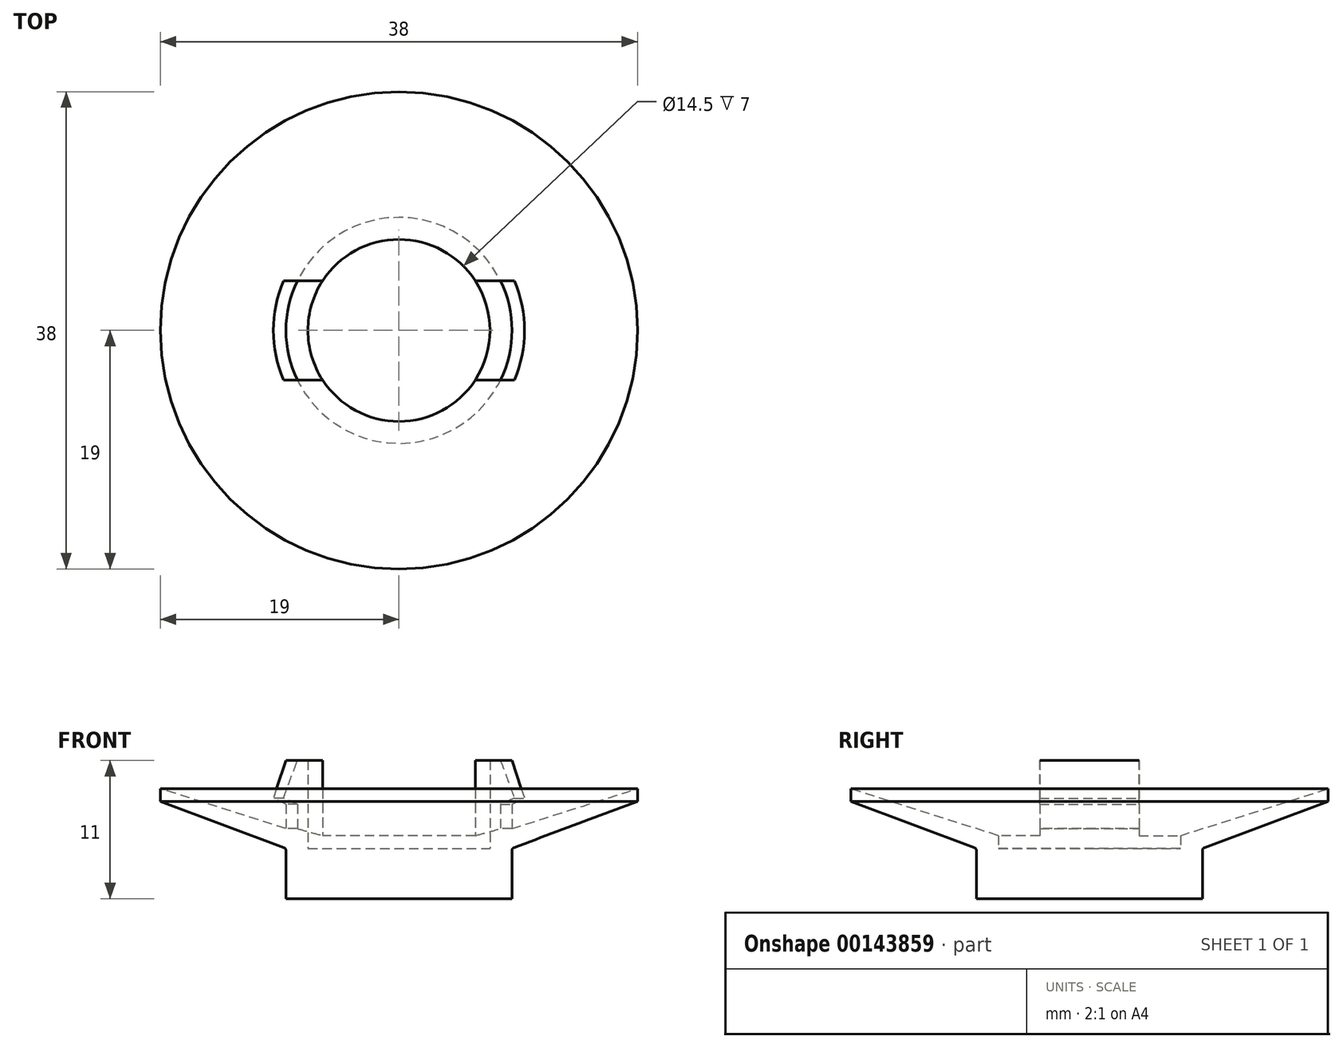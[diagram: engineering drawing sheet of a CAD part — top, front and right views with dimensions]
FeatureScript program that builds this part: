
annotation { "Feature Type Name" : "Feature", "Feature Type Description" : "" }
export const myFeature = defineFeature(function(context is Context, id is Id, definition is map)
    precondition{}
    {
        {
            var Q0;
            Q0=qCreatedBy(makeId("Front.planeOp"),FACE);
            var sketch = newSketch(context, id + "F0", { "sketchPlane" : qUnion([Q0])});
            skCircle(sketch, "E0", {"center": v(95.2, 4.49) * mm, "radius": 8.75 * mm});
            skCircle(sketch, "E1", {"center": v(95.2, -8.26) * mm, "radius": 8 * mm});
            skCircle(sketch, "E2", {"center": v(95.2, -8.26) * mm, "radius": 7.5 * mm});
            skLineSegment(sketch, "E3", {"start": v(59.96, -2.26) * mm, "end": v(59.96, -0.76) * mm});
            skLineSegment(sketch, "E4", {"start": v(59.96, -0.76) * mm, "end": v(64.96, -0.26) * mm});
            skLineSegment(sketch, "E5", {"start": v(64.96, -0.26) * mm, "end": v(64.96, -0.76) * mm});
            skLineSegment(sketch, "E6", {"start": v(64.96, -0.76) * mm, "end": v(69.96, -0.26) * mm});
            skLineSegment(sketch, "E7", {"start": v(69.96, -0.26) * mm, "end": v(69.96, -0.76) * mm});
            skLineSegment(sketch, "E8", {"start": v(69.96, -0.76) * mm, "end": v(74.96, -0.26) * mm});
            skLineSegment(sketch, "E9", {"start": v(74.96, -0.26) * mm, "end": v(86.46, -0.26) * mm});
            skLineSegment(sketch, "E10", {"start": v(86.46, -0.26) * mm, "end": v(86.46, 4.49) * mm});
            skLineSegment(sketch, "E11", {"start": v(86.46, 4.49) * mm, "end": v(76.2, 8.24) * mm});
            skLineSegment(sketch, "E12", {"start": v(76.2, 8.24) * mm, "end": v(76.2, 9.24) * mm});
            skLineSegment(sketch, "E13", {"start": v(76.2, 9.24) * mm, "end": v(95.2, 9.24) * mm});
            skLineSegment(sketch, "E14", {"start": v(95.2, 9.24) * mm, "end": v(114.2, 9.24) * mm});
            skLineSegment(sketch, "E15", {"start": v(114.2, 9.24) * mm, "end": v(114.2, 8.24) * mm});
            skLineSegment(sketch, "E16", {"start": v(114.2, 8.24) * mm, "end": v(103.96, 4.49) * mm});
            skLineSegment(sketch, "E17", {"start": v(103.96, 4.49) * mm, "end": v(103.96, -0.26) * mm});
            skLineSegment(sketch, "E18", {"start": v(103.96, -0.26) * mm, "end": v(103.18, -8.98) * mm});
            skArc(sketch, "E19", {"start": v(103.18, -8.98) * mm, "mid": v(100.6, -14.17) * mm, "end": v(95.2, -16.26) * mm});
            skLineSegment(sketch, "E20", {"start": v(95.2, -16.26) * mm, "end": v(74.96, -16.26) * mm});
            skLineSegment(sketch, "E21", {"start": v(74.96, -16.26) * mm, "end": v(69.96, -15.76) * mm});
            skLineSegment(sketch, "E22", {"start": v(69.96, -15.76) * mm, "end": v(69.96, -16.26) * mm});
            skLineSegment(sketch, "E23", {"start": v(69.96, -16.26) * mm, "end": v(64.96, -15.76) * mm});
            skLineSegment(sketch, "E24", {"start": v(64.96, -15.76) * mm, "end": v(64.96, -16.26) * mm});
            skLineSegment(sketch, "E25", {"start": v(64.96, -16.26) * mm, "end": v(59.96, -15.76) * mm});
            skLineSegment(sketch, "E26", {"start": v(59.96, -15.76) * mm, "end": v(59.96, -2.26) * mm});
            skCircle(sketch, "E27", {"center": v(95.2, 34) * mm, "radius": 6.25 * mm});
            skCircle(sketch, "E28", {"center": v(95.2, 34) * mm, "radius": 7.25 * mm});
            skCircle(sketch, "E29", {"center": v(95.2, 34) * mm, "radius": 19 * mm});
            skCircle(sketch, "E30", {"center": v(95.2, 34) * mm, "radius": 3.75 * mm});
            skLineSegment(sketch, "E31", {"start": v(86.46, 4.49) * mm, "end": v(85.46, 4.85) * mm});
            skLineSegment(sketch, "E32", {"start": v(85.46, 4.85) * mm, "end": v(85.97, 6.26) * mm});
            skLineSegment(sketch, "E33", {"start": v(85.97, 6.26) * mm, "end": v(86.97, 5.9) * mm});
            skLineSegment(sketch, "E34", {"start": v(86.97, 5.9) * mm, "end": v(86.46, 4.49) * mm});
            skCircle(sketch, "E35", {"center": v(95.2, -8.26) * mm, "radius": 6.25 * mm});
            skArc(sketch, "E36", {"start": v(104.2, 30.26) * mm, "mid": v(104.96, 34) * mm, "end": v(104.2, 37.76) * mm});
            skArc(sketch, "E37", {"start": v(86.2, 37.76) * mm, "mid": v(85.46, 34) * mm, "end": v(86.2, 30.26) * mm});
            skArc(sketch, "E38", {"start": v(103.11, 30.26) * mm, "mid": v(103.96, 34) * mm, "end": v(103.11, 37.76) * mm});
            skArc(sketch, "E39", {"start": v(87.3, 37.76) * mm, "mid": v(86.46, 34) * mm, "end": v(87.3, 30.26) * mm});
            skLineSegment(sketch, "E40", {"start": v(88.96, 4.49) * mm, "end": v(87.96, 4.49) * mm});
            skLineSegment(sketch, "E41", {"start": v(87.96, 4.49) * mm, "end": v(87.96, 11.49) * mm});
            skLineSegment(sketch, "E42", {"start": v(87.96, 11.49) * mm, "end": v(86.46, 11.49) * mm});
            skLineSegment(sketch, "E43", {"start": v(86.46, 11.49) * mm, "end": v(85.46, 8.49) * mm});
            skLineSegment(sketch, "E44", {"start": v(85.46, 8.49) * mm, "end": v(86.46, 7.99) * mm});
            skLineSegment(sketch, "E45", {"start": v(86.46, 7.99) * mm, "end": v(86.46, 6.06) * mm});
            skLineSegment(sketch, "E46", {"start": v(86.46, 6.06) * mm, "end": v(76.2, 9.24) * mm});
            skLineSegment(sketch, "E47", {"start": v(64.96, -0.76) * mm, "end": v(64.96, -15.76) * mm});
            skLineSegment(sketch, "E48", {"start": v(69.96, -0.76) * mm, "end": v(69.96, -15.76) * mm});
            skLineSegment(sketch, "E49", {"start": v(59.96, -2.01) * mm, "end": v(88.96, -2.01) * mm});
            skLineSegment(sketch, "E50", {"start": v(88.96, -2.01) * mm, "end": v(88.96, 4.49) * mm});
            skLineSegment(sketch, "E51", {"start": v(101.41, 37.76) * mm, "end": v(104.2, 37.76) * mm});
            skLineSegment(sketch, "E52", {"start": v(104.2, 30.26) * mm, "end": v(101.41, 30.26) * mm});
            skLineSegment(sketch, "E53", {"start": v(86.2, 37.76) * mm, "end": v(89, 37.76) * mm});
            skLineSegment(sketch, "E54", {"start": v(89, 30.26) * mm, "end": v(86.2, 30.26) * mm});
            skLineSegment(sketch, "E55", {"start": v(86.46, 6.06) * mm, "end": v(87.3, 6.06) * mm});
            skLineSegment(sketch, "E56", {"start": v(89, 4.49) * mm, "end": v(89, 11.49) * mm});
            skLineSegment(sketch, "E57", {"start": v(89, 11.49) * mm, "end": v(87.3, 11.49) * mm});
            skLineSegment(sketch, "E58", {"start": v(87.3, 11.49) * mm, "end": v(86.46, 8.49) * mm});
            skLineSegment(sketch, "E59", {"start": v(86.46, 8.49) * mm, "end": v(87.3, 7.99) * mm});
            skLineSegment(sketch, "E60", {"start": v(87.3, 7.99) * mm, "end": v(87.3, 6.06) * mm});
            skLineSegment(sketch, "E61", {"start": v(101.46, 4.49) * mm, "end": v(102.46, 4.49) * mm});
            skLineSegment(sketch, "E62", {"start": v(102.46, 4.49) * mm, "end": v(102.46, 11.49) * mm});
            skLineSegment(sketch, "E63", {"start": v(102.46, 11.49) * mm, "end": v(103.96, 11.49) * mm});
            skLineSegment(sketch, "E64", {"start": v(103.96, 11.49) * mm, "end": v(104.96, 8.49) * mm});
            skLineSegment(sketch, "E65", {"start": v(104.96, 8.49) * mm, "end": v(103.96, 7.99) * mm});
            skLineSegment(sketch, "E66", {"start": v(103.96, 7.99) * mm, "end": v(103.96, 6.06) * mm});
            skLineSegment(sketch, "E67", {"start": v(103.96, 6.06) * mm, "end": v(114.2, 9.24) * mm});
            skLineSegment(sketch, "E68", {"start": v(101.46, 4.49) * mm, "end": v(101.46, -8.26) * mm});
            skArc(sketch, "E69", {"start": v(101.46, -8.26) * mm, "mid": v(99.63, -12.68) * mm, "end": v(95.2, -14.51) * mm});
            skLineSegment(sketch, "E70", {"start": v(95.2, -14.51) * mm, "end": v(59.96, -14.51) * mm});
            skLineSegment(sketch, "E71", {"start": v(103.18, -8.98) * mm, "end": v(101.46, -8.98) * mm});
            skLineSegment(sketch, "E72", {"start": v(101.46, -8.98) * mm, "end": v(101.46, 4.49) * mm});
            skLineSegment(sketch, "E73", {"start": v(102.46, 4.49) * mm, "end": v(102.46, 5.59) * mm});
            skLineSegment(sketch, "E74", {"start": v(102.46, 5.59) * mm, "end": v(114.2, 9.24) * mm});
            skLineSegment(sketch, "E75", {"start": v(103.96, 7.99) * mm, "end": v(103.96, 5.4) * mm});
            skLineSegment(sketch, "E76", {"start": v(103.96, 5.4) * mm, "end": v(102.46, 3.7) * mm});
            skLineSegment(sketch, "E77", {"start": v(102.46, 3.7) * mm, "end": v(102.46, 11.49) * mm});
            skLineSegment(sketch, "E78", {"start": v(59.96, -14.51) * mm, "end": v(95.2, -14.51) * mm});
            skArc(sketch, "E79", {"start": v(95.2, -14.51) * mm, "mid": v(99.63, -12.68) * mm, "end": v(101.46, -8.26) * mm});
            skLineSegment(sketch, "E80", {"start": v(101.46, -8.26) * mm, "end": v(103.2, -8.26) * mm});
            skArc(sketch, "E81", {"start": v(103.2, -8.26) * mm, "mid": v(100.86, -13.92) * mm, "end": v(95.2, -16.26) * mm});
            skLineSegment(sketch, "E82", {"start": v(59.96, -15.76) * mm, "end": v(59.96, -14.51) * mm});
            skLineSegment(sketch, "E83", {"start": v(54, -8.26) * mm, "end": v(95.2, -8.26) * mm});
            skArc(sketch, "E84", {"start": v(95.2, -8.26) * mm, "mid": v(95.2, -8.26) * mm, "end": v(95.2, -8.26) * mm});
            skLineSegment(sketch, "E85", {"start": v(95.2, -8.26) * mm, "end": v(95.2, 13.24) * mm});
            skCircle(sketch, "E86", {"center": v(59.96, -8.26) * mm, "radius": 6.25 * mm});
            skArc(sketch, "E87", {"start": v(593.24, 411.17) * mm, "mid": v(593.34, 410.87) * mm, "end": v(593.66, 410.83) * mm});
            skArc(sketch, "E88", {"start": v(593.82, 411.03) * mm, "mid": v(593.72, 411.33) * mm, "end": v(593.4, 411.37) * mm});
            skLineSegment(sketch, "E89", {"start": v(593.83, 411.13) * mm, "end": v(594.01, 411.35) * mm});
            skLineSegment(sketch, "E90", {"start": v(593.8, 411.25) * mm, "end": v(593.93, 411.42) * mm});
            skLineSegment(sketch, "E91", {"start": v(593.72, 411.33) * mm, "end": v(593.85, 411.49) * mm});
            skLineSegment(sketch, "E92", {"start": v(593.62, 411.39) * mm, "end": v(593.76, 411.56) * mm});
            skLineSegment(sketch, "E93", {"start": v(593.5, 411.4) * mm, "end": v(593.69, 411.62) * mm});
            skLineSegment(sketch, "E94", {"start": v(59.96, -42.26) * mm, "end": v(59.96, -40.76) * mm});
            skLineSegment(sketch, "E95", {"start": v(59.96, -40.76) * mm, "end": v(64.96, -40.26) * mm});
            skLineSegment(sketch, "E96", {"start": v(64.96, -40.26) * mm, "end": v(64.96, -40.76) * mm});
            skLineSegment(sketch, "E97", {"start": v(64.96, -40.76) * mm, "end": v(69.96, -40.26) * mm});
            skLineSegment(sketch, "E98", {"start": v(69.96, -40.26) * mm, "end": v(69.96, -40.76) * mm});
            skLineSegment(sketch, "E99", {"start": v(69.96, -40.76) * mm, "end": v(74.96, -40.26) * mm});
            skLineSegment(sketch, "E100", {"start": v(74.96, -40.26) * mm, "end": v(86.46, -40.26) * mm});
            skLineSegment(sketch, "E101", {"start": v(86.46, -40.26) * mm, "end": v(86.46, -35.51) * mm});
            skLineSegment(sketch, "E102", {"start": v(86.46, -35.51) * mm, "end": v(76.2, -31.76) * mm});
            skLineSegment(sketch, "E103", {"start": v(76.2, -31.76) * mm, "end": v(76.2, -30.76) * mm});
            skLineSegment(sketch, "E104", {"start": v(76.2, -30.76) * mm, "end": v(95.2, -30.76) * mm});
            skLineSegment(sketch, "E105", {"start": v(95.2, -30.76) * mm, "end": v(114.2, -30.76) * mm});
            skLineSegment(sketch, "E106", {"start": v(114.2, -30.76) * mm, "end": v(114.2, -31.76) * mm});
            skLineSegment(sketch, "E107", {"start": v(114.2, -31.76) * mm, "end": v(103.96, -35.51) * mm});
            skLineSegment(sketch, "E108", {"start": v(103.96, -35.51) * mm, "end": v(103.96, -40.26) * mm});
            skLineSegment(sketch, "E109", {"start": v(103.96, -40.26) * mm, "end": v(103.18, -48.98) * mm});
            skArc(sketch, "E110", {"start": v(103.18, -48.98) * mm, "mid": v(100.6, -54.17) * mm, "end": v(95.2, -56.26) * mm});
            skLineSegment(sketch, "E111", {"start": v(95.2, -56.26) * mm, "end": v(74.96, -56.26) * mm});
            skLineSegment(sketch, "E112", {"start": v(74.96, -56.26) * mm, "end": v(69.96, -55.76) * mm});
            skLineSegment(sketch, "E113", {"start": v(69.96, -55.76) * mm, "end": v(69.96, -56.26) * mm});
            skLineSegment(sketch, "E114", {"start": v(69.96, -56.26) * mm, "end": v(64.96, -55.76) * mm});
            skLineSegment(sketch, "E115", {"start": v(64.96, -55.76) * mm, "end": v(64.96, -56.26) * mm});
            skLineSegment(sketch, "E116", {"start": v(64.96, -56.26) * mm, "end": v(59.96, -55.76) * mm});
            skLineSegment(sketch, "E117", {"start": v(59.96, -55.76) * mm, "end": v(59.96, -42.26) * mm});
            skLineSegment(sketch, "E118", {"start": v(86.46, -35.51) * mm, "end": v(85.46, -35.15) * mm});
            skLineSegment(sketch, "E119", {"start": v(85.46, -35.15) * mm, "end": v(85.97, -33.74) * mm});
            skLineSegment(sketch, "E120", {"start": v(85.97, -33.74) * mm, "end": v(86.97, -34.1) * mm});
            skLineSegment(sketch, "E121", {"start": v(86.97, -34.1) * mm, "end": v(86.46, -35.51) * mm});
            skLineSegment(sketch, "E122", {"start": v(88.96, -35.51) * mm, "end": v(87.96, -35.51) * mm});
            skLineSegment(sketch, "E123", {"start": v(87.96, -35.51) * mm, "end": v(87.96, -28.51) * mm});
            skLineSegment(sketch, "E124", {"start": v(87.96, -28.51) * mm, "end": v(86.46, -28.51) * mm});
            skLineSegment(sketch, "E125", {"start": v(86.46, -28.51) * mm, "end": v(85.46, -31.51) * mm});
            skLineSegment(sketch, "E126", {"start": v(85.46, -31.51) * mm, "end": v(86.46, -32.01) * mm});
            skLineSegment(sketch, "E127", {"start": v(86.46, -32.01) * mm, "end": v(86.46, -33.94) * mm});
            skLineSegment(sketch, "E128", {"start": v(86.46, -33.94) * mm, "end": v(76.2, -30.76) * mm});
            skLineSegment(sketch, "E129", {"start": v(64.96, -40.76) * mm, "end": v(64.96, -55.76) * mm});
            skLineSegment(sketch, "E130", {"start": v(69.96, -40.76) * mm, "end": v(69.96, -55.76) * mm});
            skLineSegment(sketch, "E131", {"start": v(59.96, -42.01) * mm, "end": v(88.96, -42.01) * mm});
            skLineSegment(sketch, "E132", {"start": v(88.96, -42.01) * mm, "end": v(88.96, -35.51) * mm});
            skLineSegment(sketch, "E133", {"start": v(86.46, -33.94) * mm, "end": v(87.3, -33.94) * mm});
            skLineSegment(sketch, "E134", {"start": v(89, -35.51) * mm, "end": v(89, -28.51) * mm});
            skLineSegment(sketch, "E135", {"start": v(89, -28.51) * mm, "end": v(87.3, -28.51) * mm});
            skLineSegment(sketch, "E136", {"start": v(87.3, -28.51) * mm, "end": v(86.46, -31.51) * mm});
            skLineSegment(sketch, "E137", {"start": v(86.46, -31.51) * mm, "end": v(87.3, -32.01) * mm});
            skLineSegment(sketch, "E138", {"start": v(87.3, -32.01) * mm, "end": v(87.3, -33.94) * mm});
            skLineSegment(sketch, "E139", {"start": v(101.46, -35.51) * mm, "end": v(102.46, -35.51) * mm});
            skLineSegment(sketch, "E140", {"start": v(102.46, -35.51) * mm, "end": v(102.46, -28.51) * mm});
            skLineSegment(sketch, "E141", {"start": v(102.46, -28.51) * mm, "end": v(103.96, -28.51) * mm});
            skLineSegment(sketch, "E142", {"start": v(103.96, -28.51) * mm, "end": v(104.96, -31.51) * mm});
            skLineSegment(sketch, "E143", {"start": v(104.96, -31.51) * mm, "end": v(103.96, -32.01) * mm});
            skLineSegment(sketch, "E144", {"start": v(103.96, -32.01) * mm, "end": v(103.96, -33.94) * mm});
            skLineSegment(sketch, "E145", {"start": v(103.96, -33.94) * mm, "end": v(114.2, -30.76) * mm});
            skLineSegment(sketch, "E146", {"start": v(101.46, -35.51) * mm, "end": v(101.46, -48.26) * mm});
            skArc(sketch, "E147", {"start": v(101.46, -48.26) * mm, "mid": v(99.63, -52.68) * mm, "end": v(95.2, -54.51) * mm});
            skLineSegment(sketch, "E148", {"start": v(95.2, -54.51) * mm, "end": v(59.96, -54.51) * mm});
            skLineSegment(sketch, "E149", {"start": v(103.96, -32.01) * mm, "end": v(103.96, -34.6) * mm});
            skLineSegment(sketch, "E150", {"start": v(103.96, -34.6) * mm, "end": v(102.46, -36.3) * mm});
            skLineSegment(sketch, "E151", {"start": v(102.46, -36.3) * mm, "end": v(102.46, -28.51) * mm});
            skCircle(sketch, "E152", {"center": v(59.96, -48.26) * mm, "radius": 6.25 * mm});
            skCircle(sketch, "E153", {"center": v(86.46, -38.76) * mm, "radius": 17.5 * mm});
            skLineSegment(sketch, "E154", {"start": v(55.53, -42.01) * mm, "end": v(88.96, -42.01) * mm});
            skArc(sketch, "E155", {"start": v(88.96, -42.01) * mm, "mid": v(88.96, -42.01) * mm, "end": v(88.96, -42.01) * mm});
            skLineSegment(sketch, "E156", {"start": v(88.96, -42.01) * mm, "end": v(88.96, -21.44) * mm});
            skLineSegment(sketch, "E157", {"start": v(56.96, -48.26) * mm, "end": v(95.2, -48.26) * mm});
            skLineSegment(sketch, "E158", {"start": v(95.2, -48.26) * mm, "end": v(95.2, -23.6) * mm});
            skCircle(sketch, "E159", {"center": v(74.96, -48.26) * mm, "radius": 8 * mm});
            skLineSegment(sketch, "E160", {"start": v(74.96, -42.01) * mm, "end": v(88.96, -42.01) * mm});
            skLineSegment(sketch, "E161", {"start": v(88.96, -42.01) * mm, "end": v(88.96, -38.13) * mm});
            skCircle(sketch, "E162", {"center": v(74.96, -48.26) * mm, "radius": 8.75 * mm});
            skCircle(sketch, "E163", {"center": v(103.96, 103.93) * mm, "radius": 8.75 * mm});
            skCircle(sketch, "E164", {"center": v(95.2, 95.93) * mm, "radius": 8 * mm});
            skEllipticalArc(sketch, "E165", {});
            skCircle(sketch, "E166", {"center": v(96.26, 95.94) * mm, "radius": 8.06 * mm});
            skCircle(sketch, "E167", {"center": v(97.31, 96.08) * mm, "radius": 8.12 * mm});
            skCircle(sketch, "E168", {"center": v(98.34, 96.37) * mm, "radius": 8.19 * mm});
            skCircle(sketch, "E169", {"center": v(99.33, 96.78) * mm, "radius": 8.25 * mm});
            skCircle(sketch, "E170", {"center": v(100.27, 97.33) * mm, "radius": 8.31 * mm});
            skCircle(sketch, "E171", {"center": v(101.13, 98) * mm, "radius": 8.38 * mm});
            skCircle(sketch, "E172", {"center": v(101.9, 98.8) * mm, "radius": 8.44 * mm});
            skCircle(sketch, "E173", {"center": v(102.57, 99.68) * mm, "radius": 8.5 * mm});
            skCircle(sketch, "E174", {"center": v(103.12, 100.65) * mm, "radius": 8.56 * mm});
            skCircle(sketch, "E175", {"center": v(103.54, 101.7) * mm, "radius": 8.62 * mm});
            skCircle(sketch, "E176", {"center": v(103.82, 102.8) * mm, "radius": 8.69 * mm});
            skLineSegment(sketch, "E177", {"start": v(86.2, 37.76) * mm, "end": v(104.2, 37.76) * mm, "construction": true});
            skLineSegment(sketch, "E178", {"start": v(86.2, 30.26) * mm, "end": v(104.2, 30.26) * mm, "construction": true});
            skPoint(sketch, "E179.endSnap0", {"position": v(86.46, 34) * mm});
            skCircle(sketch, "E180", {"center": v(53.16, 34) * mm, "radius": 3.05 * mm, "construction": true});
            skCircle(sketch, "E181", {"center": v(162.4, 34) * mm, "radius": 3 * mm, "construction": true});
            skLineSegment(sketch, "E182", {"start": v(53.16, 34) * mm, "end": v(162.4, 34) * mm, "construction": true});
            skLineSegment(sketch, "E183", {"start": v(95.2, 64.18) * mm, "end": v(95.2, -71.1) * mm, "construction": true});
            skLineSegment(sketch, "E184", {"start": v(110.23, 3.25) * mm, "end": v(110.23, -6.48) * mm});
            skCircle(sketch, "E185", {"center": v(0, 0) * mm, "radius": 9 * mm, "construction": true});
            skCircle(sketch, "E186", {"center": v(0, 0) * mm, "radius": 8.1 * mm, "construction": true});
            skLineSegment(sketch, "E187", {"start": v(-35.5, 0) * mm, "end": v(0, 0) * mm, "construction": true});
            skCircle(sketch, "E188", {"center": v(-35.5, 0) * mm, "radius": 7.5 * mm, "construction": true});
            skLineSegment(sketch, "E189", {"start": v(0, 8.1) * mm, "end": v(-44.33, 8.1) * mm, "construction": true});
            skLineSegment(sketch, "E190", {"start": v(0, -8.1) * mm, "end": v(-44.33, -8.1) * mm, "construction": true});
            skLineSegment(sketch, "E191", {"start": v(-35.5, 7.5) * mm, "end": v(-35.5, -7.5) * mm});
            skLineSegment(sketch, "E192", {"start": v(-13.31, 7.5) * mm, "end": v(-57.64, 7.5) * mm, "construction": true});
            skLineSegment(sketch, "E193", {"start": v(-13.38, -7.53) * mm, "end": v(-57.7, -7.53) * mm});
            skLineSegment(sketch, "E194", {"start": v(-30.5, 8.1) * mm, "end": v(-30.5, -8.1) * mm});
            skLineSegment(sketch, "E195", {"start": v(-25.5, 8.1) * mm, "end": v(-25.5, -8.1) * mm});
            skLineSegment(sketch, "E196", {"start": v(-20.5, 8.1) * mm, "end": v(-20.5, -8.17) * mm});
            skLineSegment(sketch, "E197", {"start": v(-35.5, 7.5) * mm, "end": v(-30.5, 8.1) * mm});
            skLineSegment(sketch, "E198", {"start": v(-30.5, 7.5) * mm, "end": v(-25.5, 8.1) * mm});
            skLineSegment(sketch, "E199", {"start": v(-25.5, 7.5) * mm, "end": v(-20.5, 8.1) * mm});
            skLineSegment(sketch, "E200.MirrorCS", {"start": v(-30.5, -7.5) * mm, "end": v(-25.5, -8.1) * mm});
            skLineSegment(sketch, "E201.MirrorCS", {"start": v(-35.5, -7.5) * mm, "end": v(-30.5, -8.1) * mm});
            skLineSegment(sketch, "E202.MirrorCS", {"start": v(-25.5, -7.5) * mm, "end": v(-20.5, -8.1) * mm});
            skLineSegment(sketch, "E203", {"start": v(0, 0) * mm, "end": v(0, 20.1) * mm, "construction": true});
            skLineSegment(sketch, "E204", {"start": v(-9, 0) * mm, "end": v(-9, 28.44) * mm, "construction": true});
            skLineSegment(sketch, "E205", {"start": v(-9, 8.1) * mm, "end": v(-9, 13.1) * mm});
            skLineSegment(sketch, "E206", {"start": v(-9, 13.1) * mm, "end": v(-19, 16.85) * mm});
            skLineSegment(sketch, "E207", {"start": v(-19, 16.85) * mm, "end": v(-19, 17.85) * mm});
            skLineSegment(sketch, "E208", {"start": v(-19, 17.85) * mm, "end": v(0, 17.85) * mm});
            skPoint(sketch, "E209", {"position": v(95.2, 9.24) * mm});
            skCircle(sketch, "E210", {"center": v(0, 47.85) * mm, "radius": 19 * mm});
            skCircle(sketch, "E211", {"center": v(0, 47.85) * mm, "radius": 9.75 * mm});
            skCircle(sketch, "E212", {"center": v(0, 47.85) * mm, "radius": 8.75 * mm});
            skCircle(sketch, "E213", {"center": v(0, 47.85) * mm, "radius": 7.25 * mm});
            skCircle(sketch, "E214", {"center": v(0, 47.85) * mm, "radius": 6.25 * mm});
            skLineSegment(sketch, "E215.bottom", {"start": v(-9, 13.1) * mm, "end": v(-9.94, 13.45) * mm});
            skLineSegment(sketch, "E215.top", {"start": v(-8.47, 14.5) * mm, "end": v(-9.4, 14.86) * mm});
            skLineSegment(sketch, "E215.left", {"start": v(-9, 13.1) * mm, "end": v(-8.47, 14.5) * mm});
            skLineSegment(sketch, "E215.right", {"start": v(-9.94, 13.45) * mm, "end": v(-9.4, 14.86) * mm});
            skLineSegment(sketch, "E216", {"start": v(-19, 17.85) * mm, "end": v(-7.25, 14.12) * mm});
            skLineSegment(sketch, "E217", {"start": v(-9, 14.67) * mm, "end": v(-9, 16.6) * mm});
            skLineSegment(sketch, "E218", {"start": v(-9, 16.6) * mm, "end": v(-10, 17.1) * mm});
            skLineSegment(sketch, "E219", {"start": v(-10, 17.1) * mm, "end": v(-9, 20.1) * mm});
            skLineSegment(sketch, "E220", {"start": v(-9, 20.1) * mm, "end": v(-7.25, 20.1) * mm});
            skLineSegment(sketch, "E221", {"start": v(-7.25, 20.1) * mm, "end": v(-7.25, 13.1) * mm});
            skLineSegment(sketch, "E222", {"start": v(-7.25, 13.1) * mm, "end": v(-6.25, 13.1) * mm});
            skLineSegment(sketch, "E223.MirrorCS", {"start": v(19, 16.85) * mm, "end": v(19, 17.85) * mm});
            skLineSegment(sketch, "E224.MirrorCS", {"start": v(9, 16.6) * mm, "end": v(10, 17.1) * mm});
            skLineSegment(sketch, "E225.MirrorCS", {"start": v(7.25, 13.1) * mm, "end": v(6.25, 13.1) * mm});
            skLineSegment(sketch, "E226.MirrorCS", {"start": v(19, 17.85) * mm, "end": v(0, 17.85) * mm});
            skLineSegment(sketch, "E227.MirrorCS", {"start": v(7.25, 20.1) * mm, "end": v(7.25, 13.1) * mm});
            skLineSegment(sketch, "E228.MirrorCS", {"start": v(9, 20.1) * mm, "end": v(7.25, 20.1) * mm});
            skLineSegment(sketch, "E229.MirrorCS", {"start": v(9, 13.1) * mm, "end": v(19, 16.85) * mm});
            skLineSegment(sketch, "E230.MirrorCS", {"start": v(10, 17.1) * mm, "end": v(9, 20.1) * mm});
            skLineSegment(sketch, "E231.MirrorCS", {"start": v(19, 17.85) * mm, "end": v(7.25, 14.12) * mm});
            skLineSegment(sketch, "E232.MirrorCS", {"start": v(9, 14.67) * mm, "end": v(9, 16.6) * mm});
            skLineSegment(sketch, "E233.bottom", {"start": v(12.5, 43.9) * mm, "end": v(-12.5, 43.9) * mm});
            skLineSegment(sketch, "E233.top", {"start": v(12.5, 51.8) * mm, "end": v(-12.5, 51.8) * mm});
            skLineSegment(sketch, "E233.left", {"start": v(12.5, 43.9) * mm, "end": v(12.5, 51.8) * mm});
            skLineSegment(sketch, "E233.right", {"start": v(-12.5, 43.9) * mm, "end": v(-12.5, 51.8) * mm});
            skLineSegment(sketch, "E234", {"start": v(-7.8, 43.9) * mm, "end": v(-7.8, 9.97) * mm, "construction": true});
            skLineSegment(sketch, "E235", {"start": v(-6.08, 43.9) * mm, "end": v(-6.08, 11.76) * mm, "construction": true});
            skLineSegment(sketch, "E236", {"start": v(-7.8, 20.1) * mm, "end": v(-8.91, 17.1) * mm});
            skLineSegment(sketch, "E237", {"start": v(-8.91, 17.1) * mm, "end": v(-7.8, 16.6) * mm});
            skLineSegment(sketch, "E238", {"start": v(-7.8, 16.6) * mm, "end": v(-7.8, 13.1) * mm});
            skLineSegment(sketch, "E239", {"start": v(-7.8, 13.1) * mm, "end": v(-6.08, 13.1) * mm});
            skPoint(sketch, "E239.endSnap0", {"position": v(-6.75, 13.1) * mm});
            skLineSegment(sketch, "E240", {"start": v(-6.08, 13.1) * mm, "end": v(-6.08, 20.1) * mm});
            skLineSegment(sketch, "E241", {"start": v(-6.08, 20.1) * mm, "end": v(-7.8, 20.1) * mm});
            skLineSegment(sketch, "E242", {"start": v(-9, 14.67) * mm, "end": v(-7.8, 14.67) * mm});
            skLineSegment(sketch, "E243", {"start": v(6.25, 13.1) * mm, "end": v(0, 13.1) * mm});
            skLineSegment(sketch, "E244", {"start": v(0, 9.1) * mm, "end": v(9, 9.1) * mm});
            skLineSegment(sketch, "E245", {"start": v(9, 9.1) * mm, "end": v(9, 13.1) * mm});
            skLineSegment(sketch, "E246", {"start": v(7.25, 13.1) * mm, "end": v(9, 13.66) * mm});
            skLineSegment(sketch, "E247", {"start": v(9, 13.66) * mm, "end": v(9, 14.67) * mm});
            skLineSegment(sketch, "E248", {"start": v(0, 13.1) * mm, "end": v(0, 8.1) * mm});
            skLineSegment(sketch, "E249", {"start": v(7.25, 14.12) * mm, "end": v(7.25, 13.1) * mm});
            skLineSegment(sketch, "E250", {"start": v(-20.5, 8.1) * mm, "end": v(-10, 8.1) * mm});
            skLineSegment(sketch, "E251", {"start": v(-10, 8.1) * mm, "end": v(-10, -8.1) * mm});
            skLineSegment(sketch, "E252", {"start": v(-10, -8.1) * mm, "end": v(-20.5, -8.1) * mm});
            const initialGuessF0  = {"E165": [0.09520800700000001, 0.10392969999999999, 1, 0, 0.0175, 0.016, 4.71238898038469, 0]};
            skSetInitialGuess(sketch, initialGuessF0);
            skSolve(sketch);
        }
        {
            var Q0;
            {var subQ5=sQuery(id+"F0.wireOp",EDGE,"E228.MirrorCS");Q0=makeQuery(id+"F0.imprint","IMPRINT",FACE,{"disambiguationData":[TD([[makeQuery(id+"F0.imprint","IMPRINT",EDGE,{"derivedFrom":subQ5}),1.0]])]});}
            var Q1;
            {var subQ1=sQuery(id+"F0.wireOp",EDGE,"E224.MirrorCS");Q1=makeQuery(id+"F0.imprint","IMPRINT",FACE,{"disambiguationData":[TD([[makeQuery(id+"F0.imprint","IMPRINT",EDGE,{"derivedFrom":subQ1}),1.0]])]});}
            var Q2;
            {var subQ0=sQuery(id+"F0.wireOp",EDGE,"E246");Q2=makeQuery(id+"F0.imprint","IMPRINT",FACE,{"disambiguationData":[TD([[makeQuery(id+"F0.imprint","IMPRINT",EDGE,{"derivedFrom":subQ0}),1.0]])]});}
            var Q3;
            Q3=sQuery(id+"F0.wireOp",EDGE,"E203");
            revolve(context, id + "F1", {"entities" : qUnion([Q0, Q1, Q2]), "axis" : qUnion([Q3]), "revolveType" : RevolveType.FULL});
        }
        {
            var Q0;
            Q0=qCreatedBy(makeId("Top.planeOp"),FACE);
            var sketch = newSketch(context, id + "F2", { "sketchPlane" : qUnion([Q0])});
            skLineSegment(sketch, "E253.bottom", {"start": v(12.5, -3.95) * mm, "end": v(-12.5, -3.95) * mm});
            skLineSegment(sketch, "E253.top", {"start": v(12.5, 3.95) * mm, "end": v(-12.5, 3.95) * mm});
            skLineSegment(sketch, "E253.left", {"start": v(12.5, -3.95) * mm, "end": v(12.5, 3.95) * mm});
            skLineSegment(sketch, "E253.right", {"start": v(-12.5, -3.95) * mm, "end": v(-12.5, 3.95) * mm});
            skPoint(sketch, "E253.middle", {"position": v(0, 0) * mm});
            skSolve(sketch);
        }
        {
            var Q0;
            Q0=makeQuery(id+"F2.imprint","IMPRINT",FACE,{"disambiguationData":[TD([[makeQuery(id+"F2.imprint","IMPRINT",EDGE,{"derivedFrom":sQuery(id+"F2.wireOp",EDGE,"E253.bottom")}),-1.0]])]});
            extrude(context, id + "F3", {"entities" : qUnion([Q0]), "operationType" : NewBodyOperationType.INTERSECT, "depth" : 25 * mm});
        }
        {
            var Q0;
            {var subQ1=sQuery(id+"F0.wireOp",EDGE,"E223.MirrorCS");Q0=makeQuery(id+"F0.imprint","IMPRINT",FACE,{"disambiguationData":[TD([[makeQuery(id+"F0.imprint","IMPRINT",EDGE,{"derivedFrom":subQ1}),1.0]])]});}
            var Q1;
            Q1=makeQuery(id+"F0.imprint","IMPRINT",FACE,{"disambiguationData":[TD([[makeQuery(id+"F0.imprint","IMPRINT",EDGE,{"derivedFrom":sQuery(id+"F0.wireOp",EDGE,"E246")}),1.0]])]});
            var Q2;
            Q2=sQuery(id+"F0.wireOp",EDGE,"E248");
            revolve(context, id + "F4", {"operationType" : NewBodyOperationType.ADD, "entities" : qUnion([Q0, Q1]), "axis" : qUnion([Q2]), "revolveType" : RevolveType.FULL});
        }
        {
            var Q0;
            Q0=makeQuery(id+"F4.opRevolve","SWEPT_EDGE",EDGE,{"disambiguationData":[OSD([sQuery(id+"F0.wireOp",EDGE,"E229.MirrorCS"),sQuery(id+"F0.wireOp",EDGE,"E245")])]});
            fillet(context, id + "F5", {"entities" : qUnion([Q0]), "radius" : .25 * mm, "tangentPropagation" : true, "allowEdgeOverflow" : false});
        }
    });
